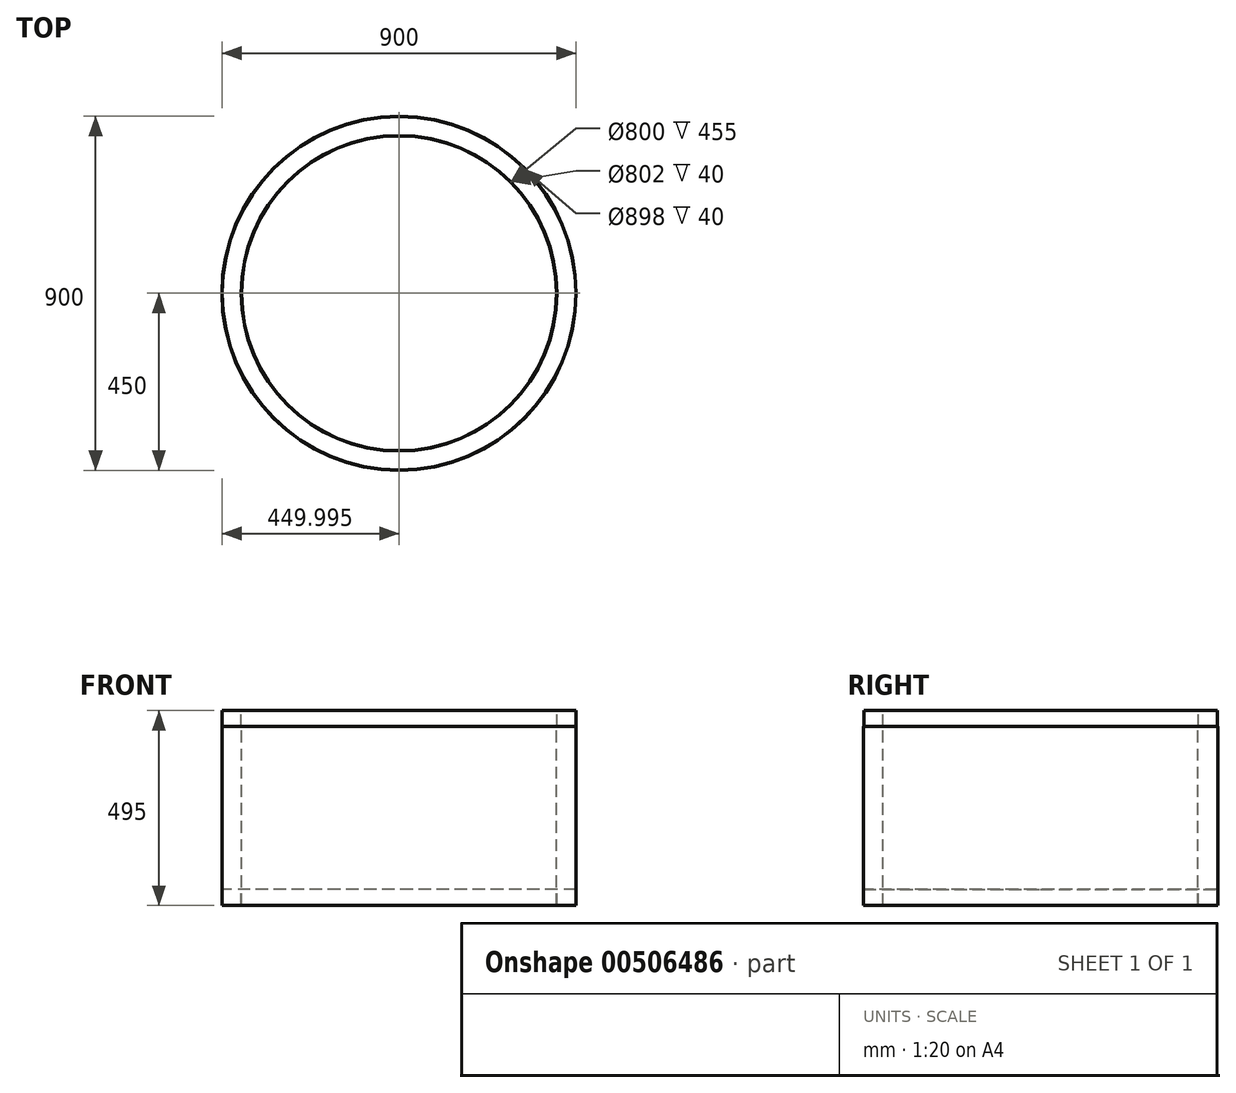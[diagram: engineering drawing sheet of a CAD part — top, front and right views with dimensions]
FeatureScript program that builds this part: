
annotation { "Feature Type Name" : "Feature", "Feature Type Description" : "" }
export const myFeature = defineFeature(function(context is Context, id is Id, definition is map)
    precondition{}
    {
        {
            var Q0;
            Q0=qCreatedBy(makeId("Front.planeOp"),FACE);
            var sketch = newSketch(context, id + "F0", { "sketchPlane" : qUnion([Q0])});
            skLineSegment(sketch, "E0", {"start": v(0, 74.87) * mm, "end": v(0, -73.71) * mm, "construction": true});
            skLineSegment(sketch, "E1", {"start": v(281.2, 374.84) * mm, "end": v(281.2, -528.94) * mm, "construction": true});
            skLineSegment(sketch, "E2", {"start": v(-118.8, -489.75) * mm, "end": v(-118.8, -34.75) * mm});
            skLineSegment(sketch, "E3", {"start": v(-118.8, -34.75) * mm, "end": v(-119.8, -34.75) * mm});
            skLineSegment(sketch, "E4", {"start": v(-119.8, -34.75) * mm, "end": v(-119.8, 5.25) * mm});
            skLineSegment(sketch, "E5", {"start": v(-119.8, 5.25) * mm, "end": v(-167.8, 5.25) * mm});
            skLineSegment(sketch, "E6", {"start": v(-167.8, 5.25) * mm, "end": v(-167.8, -34.75) * mm});
            skLineSegment(sketch, "E7", {"start": v(-167.8, -34.75) * mm, "end": v(-168.8, -34.75) * mm});
            skLineSegment(sketch, "E8", {"start": v(-168.8, -34.75) * mm, "end": v(-168.8, -489.75) * mm});
            skLineSegment(sketch, "E9", {"start": v(-168.8, -489.75) * mm, "end": v(-167.8, -489.75) * mm});
            skLineSegment(sketch, "E10", {"start": v(-167.8, -489.75) * mm, "end": v(-167.8, -449.75) * mm});
            skLineSegment(sketch, "E11", {"start": v(-167.8, -449.75) * mm, "end": v(-119.8, -449.75) * mm});
            skLineSegment(sketch, "E12", {"start": v(-119.8, -449.75) * mm, "end": v(-119.8, -489.75) * mm});
            skLineSegment(sketch, "E13", {"start": v(-119.8, -489.75) * mm, "end": v(-118.8, -489.75) * mm});
            skSolve(sketch);
        }
        {
            var Q0;
            Q0=qSketchRegion(id+"F0",true);
            var Q1;
            Q1=sQuery(id+"F0.wireOp",EDGE,"E1");
            revolve(context, id + "F1", {"entities" : qUnion([Q0]), "axis" : qUnion([Q1]), "revolveType" : RevolveType.FULL});
        }
    });
